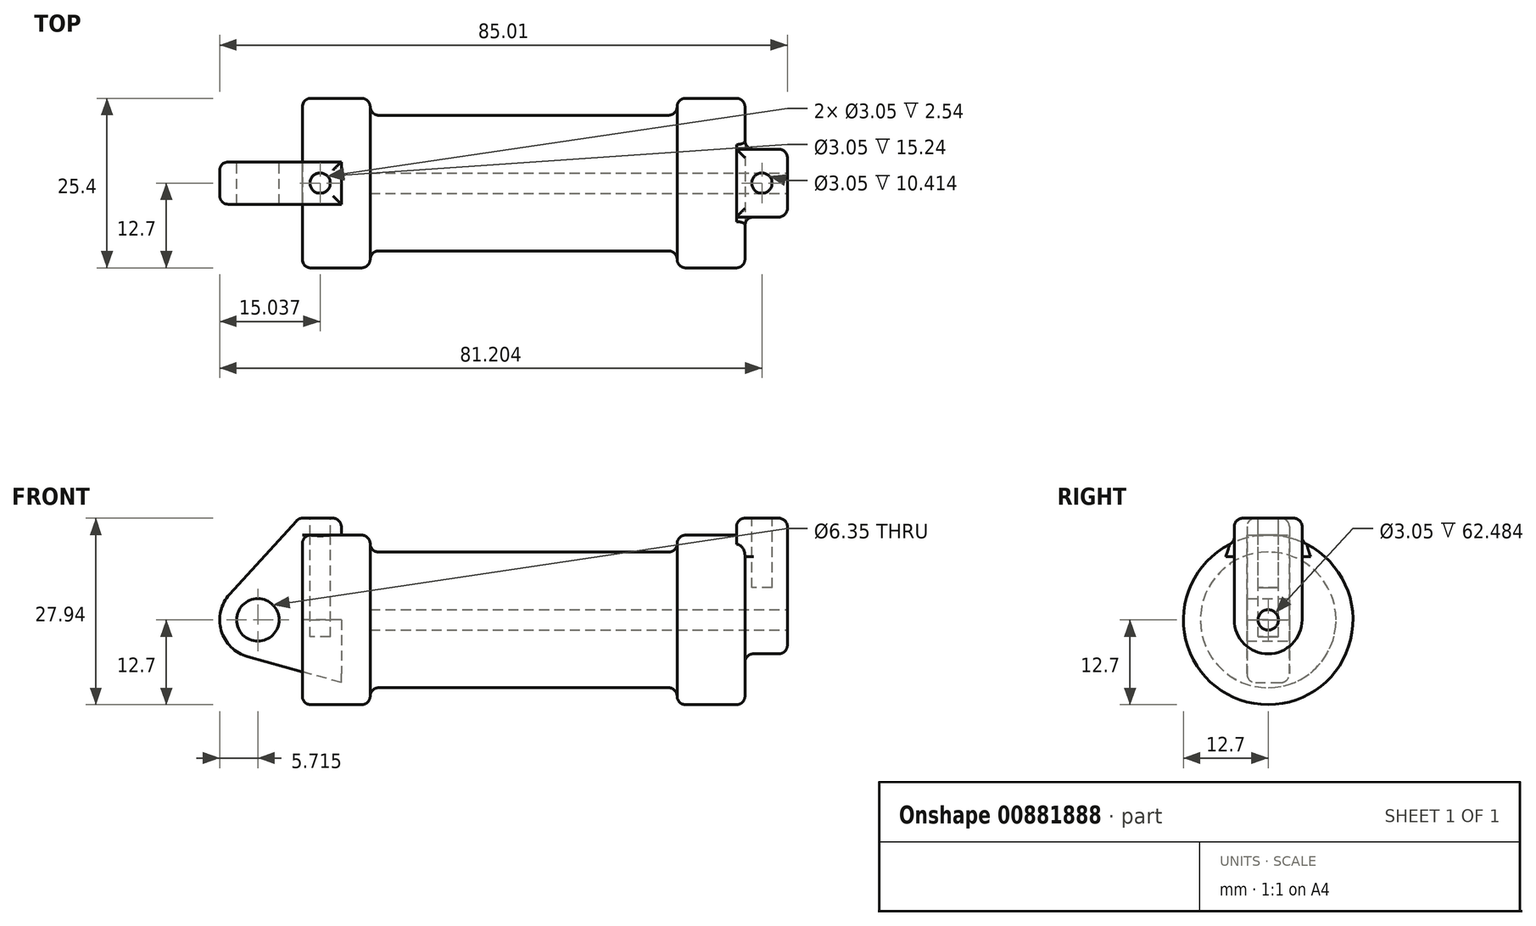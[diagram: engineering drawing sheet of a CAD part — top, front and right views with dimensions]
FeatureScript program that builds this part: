
annotation { "Feature Type Name" : "Feature", "Feature Type Description" : "" }
export const myFeature = defineFeature(function(context is Context, id is Id, definition is map)
    precondition{}
    {
        {
            var Q0;
            Q0=qCreatedBy(makeId("Front.planeOp"),FACE);
            var sketch = newSketch(context, id + "F0", { "sketchPlane" : qUnion([Q0])});
            skLineSegment(sketch, "E0", {"start": v(0, 0) * mm, "end": v(0, 12.7) * mm});
            skLineSegment(sketch, "E1", {"start": v(0, 12.7) * mm, "end": v(10.16, 12.7) * mm});
            skLineSegment(sketch, "E2", {"start": v(10.16, 12.7) * mm, "end": v(10.16, 10.16) * mm});
            skLineSegment(sketch, "E3", {"start": v(10.16, 10.16) * mm, "end": v(56.13, 10.16) * mm});
            skLineSegment(sketch, "E4", {"start": v(56.13, 10.16) * mm, "end": v(56.13, 12.7) * mm});
            skLineSegment(sketch, "E5", {"start": v(56.13, 12.7) * mm, "end": v(66.3, 12.7) * mm});
            skLineSegment(sketch, "E6", {"start": v(66.3, 12.7) * mm, "end": v(66.3, 0) * mm});
            skLineSegment(sketch, "E7", {"start": v(66.3, 0) * mm, "end": v(0, 0) * mm});
            skLineSegment(sketch, "E8", {"start": v(5.84, 15.24) * mm, "end": v(-0.5, 15.24) * mm});
            skLineSegment(sketch, "E9", {"start": v(-0.5, 15.24) * mm, "end": v(-10.88, 3.85) * mm});
            skLineSegment(sketch, "E10", {"start": v(0, 0) * mm, "end": v(-6.65, 0) * mm});
            skCircle(sketch, "E11", {"center": v(-6.65, 0) * mm, "radius": 5.72 * mm});
            skCircle(sketch, "E12", {"center": v(-6.65, 0) * mm, "radius": 3.18 * mm});
            skLineSegment(sketch, "E13", {"start": v(5.84, 15.24) * mm, "end": v(5.84, -9.4) * mm});
            skLineSegment(sketch, "E14", {"start": v(5.84, -9.4) * mm, "end": v(-8.18, -5.5) * mm});
            skSolve(sketch);
        }
        {
            var Q0;
            {var subQ0=sQuery(id+"F0.wireOp",EDGE,"E2");Q0=makeQuery(id+"F0.imprint","IMPRINT",FACE,{"disambiguationData":[TD([[makeQuery(id+"F0.imprint","IMPRINT",EDGE,{"derivedFrom":subQ0}),-1.0]])]});}
            var Q1;
            {var subQ0=sQuery(id+"F0.wireOp",EDGE,"E0");Q1=makeQuery(id+"F0.imprint","IMPRINT",FACE,{"disambiguationData":[TD([[makeQuery(id+"F0.imprint","IMPRINT",EDGE,{"derivedFrom":subQ0}),-1.0]])]});}
            var Q2;
            Q2=sQuery(id+"F0.wireOp",EDGE,"E7");
            revolve(context, id + "F1", {"surfaceOperationType" : NewSurfaceOperationType.NEW, "entities" : qUnion([Q0, Q1]), "axis" : qUnion([Q2]), "revolveType" : RevolveType.FULL});
        }
        {
            var Q0;
            {var subQ0=sQuery(id+"F0.wireOp",EDGE,"E14");Q0=makeQuery(id+"F0.imprint","IMPRINT",FACE,{"disambiguationData":[TD([[makeQuery(id+"F0.imprint","IMPRINT",EDGE,{"derivedFrom":subQ0}),-1.0]])]});}
            var Q1;
            {var subQ5=sQuery(id+"F0.wireOp",EDGE,"E12");Q1=makeQuery(id+"F0.imprint","IMPRINT",FACE,{"disambiguationData":[TD([[makeQuery(id+"F0.imprint","IMPRINT",EDGE,{"derivedFrom":subQ5}),-1.0]])]});}
            var Q2;
            {var subQ1=sQuery(id+"F0.wireOp",EDGE,"E0");Q2=makeQuery(id+"F0.imprint","IMPRINT",FACE,{"disambiguationData":[TD([[makeQuery(id+"F0.imprint","IMPRINT",EDGE,{"derivedFrom":subQ1}),1.0]])]});}
            extrude(context, id + "F2", {"entities" : qUnion([Q0, Q1, Q2]), "endBound" : BoundingType.SYMMETRIC, "depth" : 6.35 * mm, "offsetDistance" : 25.4 * mm});
        }
        {
            var Q0;
            Q0=makeQuery(id+"F1.opRevolve","SWEPT_FACE",FACE,{"disambiguationData":[OSD([sQuery(id+"F0.wireOp",EDGE,"E6")])]});
            var sketch = newSketch(context, id + "F3", { "sketchPlane" : qUnion([Q0])});
            skCircle(sketch, "E15", {"center": v(0, 0) * mm, "radius": 1.52 * mm});
            skCircle(sketch, "E16", {"center": v(0, 0) * mm, "radius": 5.08 * mm});
            skLineSegment(sketch, "E17", {"start": v(5.08, 0) * mm, "end": v(5.08, 15.24) * mm});
            skLineSegment(sketch, "E18", {"start": v(-5.08, 0) * mm, "end": v(-5.08, 15.24) * mm});
            skLineSegment(sketch, "E19", {"start": v(-5.08, 15.24) * mm, "end": v(5.08, 15.24) * mm});
            skSolve(sketch);
        }
        {
            var Q0;
            Q0=makeQuery(id+"F3.imprint","IMPRINT",FACE,{"disambiguationData":[TD([[makeQuery(id+"F3.imprint","IMPRINT",EDGE,{"derivedFrom":sQuery(id+"F3.wireOp",EDGE,"E15")}),1.0]])]});
            var Q1;
            Q1=makeQuery(id+"F1.opRevolve","SWEPT_FACE",FACE,{"disambiguationData":[OSD([sQuery(id+"F0.wireOp",EDGE,"E2")])]});
            extrude(context, id + "F4", {"entities" : qUnion([Q0]), "operationType" : NewBodyOperationType.REMOVE, "endBound" : BoundingType.UP_TO_SURFACE, "oppositeDirection" : true, "depth" : 25.4 * mm, "endBoundEntityFace" : qUnion([Q1]), "offsetDistance" : 25.4 * mm});
        }
        {
            var Q0;
            {var subQ0=sQuery(id+"F3.wireOp",EDGE,"E19");Q0=makeQuery(id+"F3.imprint","IMPRINT",FACE,{"disambiguationData":[TD([[makeQuery(id+"F3.imprint","IMPRINT",EDGE,{"derivedFrom":subQ0}),-1.0]])]});}
            var Q1;
            {var subQ0=sQuery(id+"F3.wireOp",EDGE,"E17");var subQ1=sQuery(id+"F3.wireOp",EDGE,"E16");var subQ2=makeQuery(id+"F3.imprint","INTERSECT",VERTEX,{"derivedFrom":[subQ1,subQ0]});Q1=makeQuery(id+"F3.imprint","IMPRINT",FACE,{"disambiguationData":[TD([[makeQuery(id+"F3.imprint","IMPRINT",EDGE,{"disambiguationData":[TD([[subQ2,-1.0]])],"derivedFrom":subQ1}),-1.0]])]});}
            var Q2;
            Q2=makeQuery(id+"F3.imprint","IMPRINT",FACE,{"disambiguationData":[TD([[makeQuery(id+"F3.imprint","IMPRINT",EDGE,{"derivedFrom":sQuery(id+"F3.wireOp",EDGE,"E15")}),-1.0]])]});
            extrude(context, id + "F5", {"entities" : qUnion([Q0, Q1, Q2]), "oppositeDirection" : true, "depth" : 1.27 * mm, "offsetDistance" : 25.4 * mm});
        }
        {
            var Q0;
            {var subQ0=sQuery(id+"F3.wireOp",EDGE,"E19");Q0=makeQuery(id+"F3.imprint","IMPRINT",FACE,{"disambiguationData":[TD([[makeQuery(id+"F3.imprint","IMPRINT",EDGE,{"derivedFrom":subQ0}),-1.0]])]});}
            var Q1;
            {var subQ0=sQuery(id+"F3.wireOp",EDGE,"E17");var subQ1=sQuery(id+"F3.wireOp",EDGE,"E16");var subQ2=makeQuery(id+"F3.imprint","INTERSECT",VERTEX,{"derivedFrom":[subQ1,subQ0]});Q1=makeQuery(id+"F3.imprint","IMPRINT",FACE,{"disambiguationData":[TD([[makeQuery(id+"F3.imprint","IMPRINT",EDGE,{"disambiguationData":[TD([[subQ2,-1.0]])],"derivedFrom":subQ1}),-1.0]])]});}
            var Q2;
            Q2=makeQuery(id+"F3.imprint","IMPRINT",FACE,{"disambiguationData":[TD([[makeQuery(id+"F3.imprint","IMPRINT",EDGE,{"derivedFrom":sQuery(id+"F3.wireOp",EDGE,"E15")}),-1.0]])]});
            extrude(context, id + "F6", {"entities" : qUnion([Q0, Q1, Q2]), "operationType" : NewBodyOperationType.ADD, "depth" : 6.35 * mm, "offsetDistance" : 25.4 * mm});
        }
        {
            var Q0;
            Q0=makeQuery(id+"F2.opExtrude","SWEPT_FACE",FACE,{"disambiguationData":[OSD([sQuery(id+"F0.wireOp",EDGE,"E8")])]});
            var sketch = newSketch(context, id + "F7", { "sketchPlane" : qUnion([Q0])});
            skCircle(sketch, "E20", {"center": v(2.67, 0) * mm, "radius": 1.52 * mm});
            skPoint(sketch, "E20.centerSnap0", {"position": v(-0.5, 0) * mm});
            skPoint(sketch, "E20.centerSnap1", {"position": v(2.67, 3.18) * mm});
            skSolve(sketch);
        }
        {
            var Q0;
            {var subQ0=sQuery(id+"F3.wireOp",EDGE,"E19");Q0=makeQuery(id+"F6.boolean.opBoolean","MERGE",FACE,{"derivedFrom":[makeQuery(id+"F5.opExtrude","SWEPT_FACE",FACE,{"disambiguationData":[OSD([subQ0])]}),makeQuery(id+"F6.opExtrude","SWEPT_FACE",FACE,{"disambiguationData":[OSD([subQ0])]})]});}
            var sketch = newSketch(context, id + "F8", { "sketchPlane" : qUnion([Q0])});
            skCircle(sketch, "E21", {"center": v(68.83, 0) * mm, "radius": 1.52 * mm});
            skPoint(sketch, "E21.centerSnap0", {"position": v(68.83, 5.08) * mm});
            skPoint(sketch, "E21.centerSnap1", {"position": v(65.02, 0) * mm});
            skSolve(sketch);
        }
        {
            var Q0;
            Q0=makeQuery(id+"F7.imprint","IMPRINT",FACE,{"disambiguationData":[TD([[makeQuery(id+"F7.imprint","IMPRINT",EDGE,{"derivedFrom":sQuery(id+"F7.wireOp",EDGE,"E20")}),1.0]])]});
            extrude(context, id + "F9", {"entities" : qUnion([Q0]), "operationType" : NewBodyOperationType.REMOVE, "oppositeDirection" : true, "depth" : 17.78 * mm, "offsetDistance" : 25.4 * mm});
        }
        {
            var Q0;
            Q0=makeQuery(id+"F8.imprint","IMPRINT",FACE,{"disambiguationData":[TD([[makeQuery(id+"F8.imprint","IMPRINT",EDGE,{"derivedFrom":sQuery(id+"F8.wireOp",EDGE,"E21")}),1.0]])]});
            extrude(context, id + "F10", {"entities" : qUnion([Q0]), "operationType" : NewBodyOperationType.REMOVE, "oppositeDirection" : true, "depth" : 10.4 * mm, "offsetDistance" : 25.4 * mm});
        }
        {
            var Q0;
            Q0=makeQuery(id+"F1.opRevolve","SWEPT_EDGE",EDGE,{"disambiguationData":[OSD([sQuery(id+"F0.wireOp",EDGE,"E2"),sQuery(id+"F0.wireOp",EDGE,"E3")])]});
            var Q1;
            Q1=makeQuery(id+"F1.opRevolve","SWEPT_EDGE",EDGE,{"disambiguationData":[OSD([sQuery(id+"F0.wireOp",EDGE,"E3"),sQuery(id+"F0.wireOp",EDGE,"E4")])]});
            fillet(context, id + "F11", {"entities" : qUnion([Q0, Q1]), "radius" : 1.27 * mm, "tangentPropagation" : true, "allowEdgeOverflow" : false});
        }
        {
            var Q0;
            Q0=makeQuery(id+"F1.opRevolve","SWEPT_EDGE",EDGE,{"disambiguationData":[OSD([sQuery(id+"F0.wireOp",EDGE,"E1"),sQuery(id+"F0.wireOp",EDGE,"E2")])]});
            var Q1;
            Q1=makeQuery(id+"F2.opExtrude","CAP_EDGE",EDGE,{"disambiguationData":[OSD([sQuery(id+"F0.wireOp",EDGE,"E8")])],"isStart":false});
            var Q2;
            Q2=makeQuery(id+"F2.opExtrude","SWEPT_EDGE",EDGE,{"disambiguationData":[OSD([sQuery(id+"F0.wireOp",EDGE,"E8"),sQuery(id+"F0.wireOp",EDGE,"E13")])]});
            var Q3;
            Q3=makeQuery(id+"F2.opExtrude","CAP_EDGE",EDGE,{"disambiguationData":[OSD([sQuery(id+"F0.wireOp",EDGE,"E8")])],"isStart":true});
            var Q4;
            Q4=makeQuery(id+"F2.opExtrude","SWEPT_EDGE",EDGE,{"disambiguationData":[OSD([sQuery(id+"F0.wireOp",EDGE,"E8"),sQuery(id+"F0.wireOp",EDGE,"E9")])]});
            var Q5;
            Q5=makeQuery(id+"F1.opRevolve","SWEPT_EDGE",EDGE,{"disambiguationData":[OSD([sQuery(id+"F0.wireOp",EDGE,"E0"),sQuery(id+"F0.wireOp",EDGE,"E1")])]});
            var Q6;
            Q6=makeQuery(id+"F2.opExtrude","CAP_EDGE",EDGE,{"disambiguationData":[OSD([sQuery(id+"F0.wireOp",EDGE,"E9")])],"isStart":false});
            var Q7;
            Q7=makeQuery(id+"F2.opExtrude","CAP_EDGE",EDGE,{"disambiguationData":[OSD([sQuery(id+"F0.wireOp",EDGE,"E11")])],"isStart":false});
            var Q8;
            Q8=makeQuery(id+"F2.opExtrude","CAP_EDGE",EDGE,{"disambiguationData":[OSD([sQuery(id+"F0.wireOp",EDGE,"E11")])],"isStart":true});
            var Q9;
            Q9=makeQuery(id+"F2.opExtrude","CAP_EDGE",EDGE,{"disambiguationData":[OSD([sQuery(id+"F0.wireOp",EDGE,"E14")])],"isStart":true});
            fillet(context, id + "F12", {"entities" : qUnion([Q0, Q1, Q2, Q3, Q4, Q5, Q6, Q7, Q8, Q9]), "radius" : 1.27 * mm, "tangentPropagation" : true, "allowEdgeOverflow" : false});
        }
        {
            var Q0;
            Q0=makeQuery(id+"F1.opRevolve","SWEPT_EDGE",EDGE,{"disambiguationData":[OSD([sQuery(id+"F0.wireOp",EDGE,"E5"),sQuery(id+"F0.wireOp",EDGE,"E6")])]});
            var Q1;
            {var subQ0=sQuery(id+"F3.wireOp",EDGE,"E19");var subQ1=sQuery(id+"F3.wireOp",EDGE,"E18");Q1=makeQuery(id+"F6.boolean.opBoolean","MERGE",EDGE,{"derivedFrom":[makeQuery(id+"F5.opExtrude","SWEPT_EDGE",EDGE,{"disambiguationData":[OSD([subQ1,subQ0])]}),makeQuery(id+"F6.opExtrude","SWEPT_EDGE",EDGE,{"disambiguationData":[OSD([subQ1,subQ0])]})]});}
            var Q2;
            Q2=makeQuery(id+"F5.opExtrude","CAP_EDGE",EDGE,{"disambiguationData":[OSD([sQuery(id+"F3.wireOp",EDGE,"E19")])],"isStart":false});
            var Q3;
            {var subQ0=sQuery(id+"F3.wireOp",EDGE,"E19");var subQ1=sQuery(id+"F3.wireOp",EDGE,"E17");Q3=makeQuery(id+"F6.boolean.opBoolean","MERGE",EDGE,{"derivedFrom":[makeQuery(id+"F5.opExtrude","SWEPT_EDGE",EDGE,{"disambiguationData":[OSD([subQ1,subQ0])]}),makeQuery(id+"F6.opExtrude","SWEPT_EDGE",EDGE,{"disambiguationData":[OSD([subQ1,subQ0])]})]});}
            var Q4;
            Q4=makeQuery(id+"F6.opExtrude","CAP_EDGE",EDGE,{"disambiguationData":[OSD([sQuery(id+"F3.wireOp",EDGE,"E18")])],"isStart":false});
            var Q5;
            Q5=makeQuery(id+"F6.opExtrude","CAP_EDGE",EDGE,{"disambiguationData":[OSD([sQuery(id+"F3.wireOp",EDGE,"E19")])],"isStart":false});
            var Q6;
            Q6=makeQuery(id+"F6.boolean.opBoolean","INTERSECT",EDGE,{"derivedFrom":[makeQuery(id+"F1.opRevolve","SWEPT_FACE",FACE,{"disambiguationData":[OSD([sQuery(id+"F0.wireOp",EDGE,"E6")])]}),makeQuery(id+"F6.opExtrude","SWEPT_FACE",FACE,{"disambiguationData":[OSD([sQuery(id+"F3.wireOp",EDGE,"E18")])]})]});
            var Q7;
            Q7=makeQuery(id+"F1.opRevolve","SWEPT_EDGE",EDGE,{"disambiguationData":[OSD([sQuery(id+"F0.wireOp",EDGE,"E4"),sQuery(id+"F0.wireOp",EDGE,"E5")])]});
            fillet(context, id + "F13", {"entities" : qUnion([Q0, Q1, Q2, Q3, Q4, Q5, Q6, Q7]), "radius" : 1.27 * mm, "tangentPropagation" : true, "allowEdgeOverflow" : false});
        }
    });
